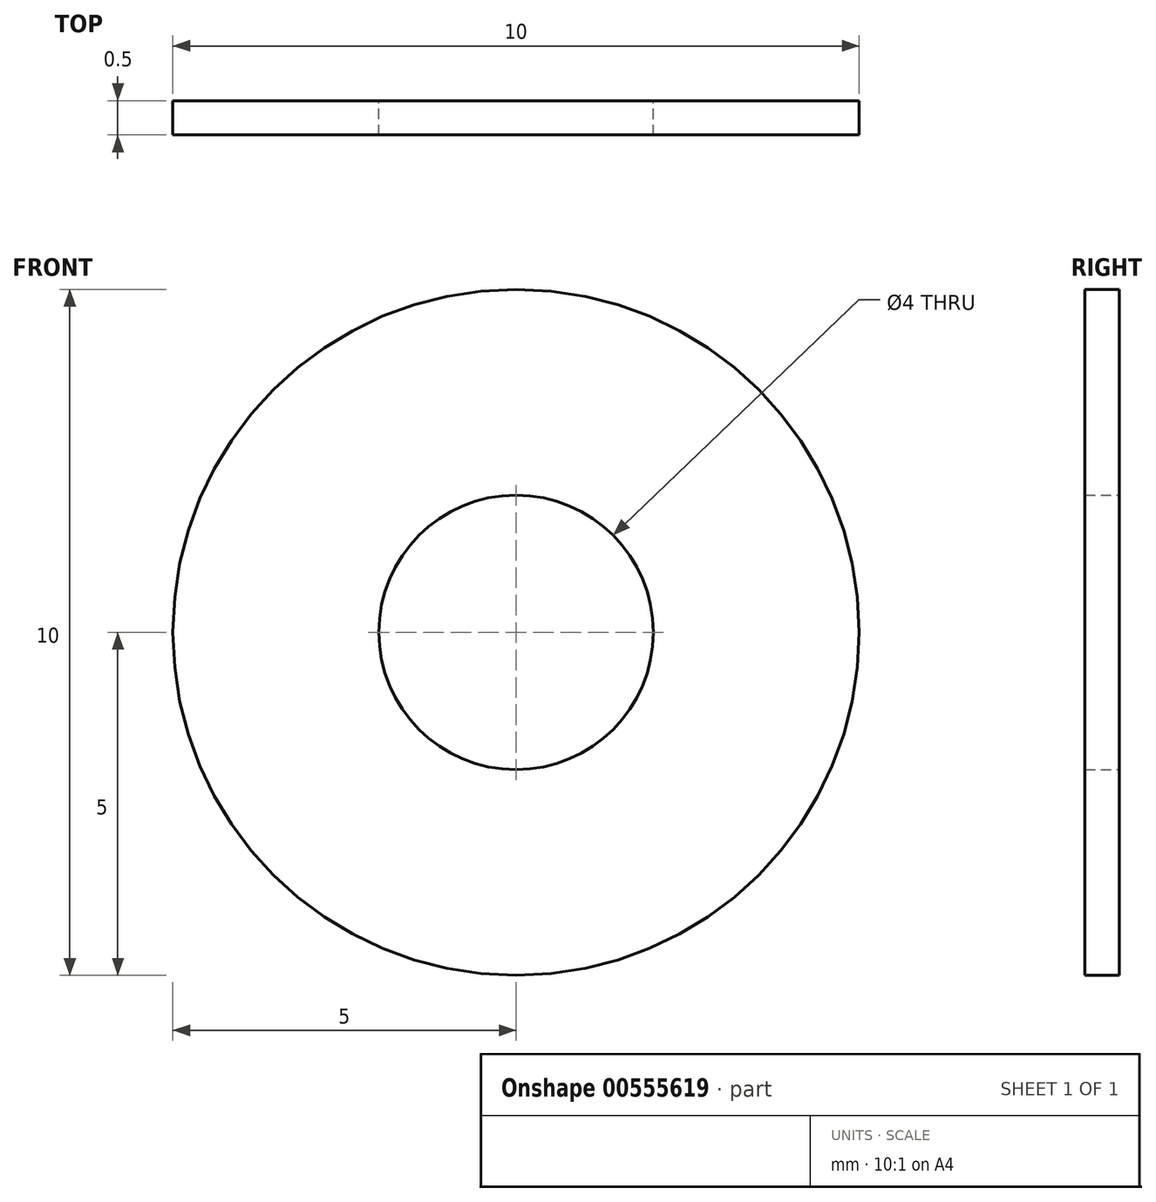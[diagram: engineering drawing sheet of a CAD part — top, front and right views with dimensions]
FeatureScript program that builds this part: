
annotation { "Feature Type Name" : "Feature", "Feature Type Description" : "" }
export const myFeature = defineFeature(function(context is Context, id is Id, definition is map)
    precondition{}
    {
        {
            var Q0;
            Q0=qCreatedBy(makeId("Front.planeOp"),FACE);
            var sketch = newSketch(context, id + "F0", { "sketchPlane" : qUnion([Q0])});
            skCircle(sketch, "E0", {"center": v(0, 0) * mm, "radius": 2 * mm});
            skCircle(sketch, "E1", {"center": v(0, 0) * mm, "radius": 5 * mm});
            skSolve(sketch);
        }
        {
            var Q0;
            Q0 = qSketchRegion(id + "F0", true);
            extrude(context, id + "F1", {"entities" : qUnion([Q0]), "depth" : .5 * mm, "offsetDistance" : 25 * mm});
        }
    });
